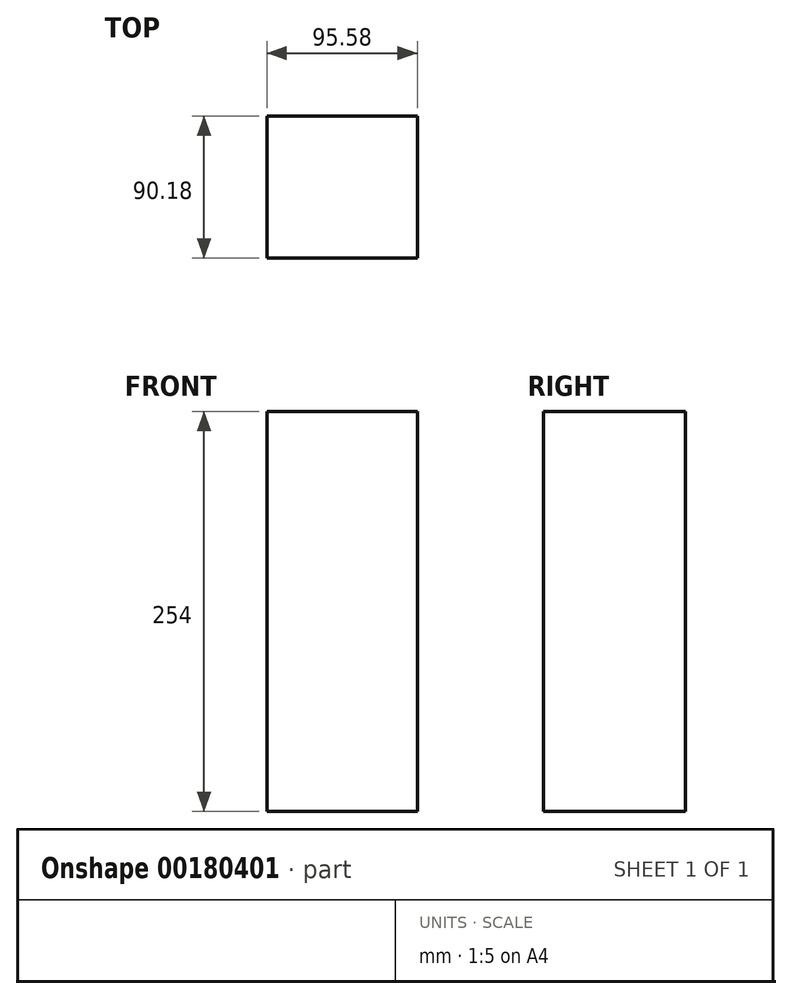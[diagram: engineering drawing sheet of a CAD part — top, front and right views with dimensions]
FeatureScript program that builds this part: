
annotation { "Feature Type Name" : "Feature", "Feature Type Description" : "" }
export const myFeature = defineFeature(function(context is Context, id is Id, definition is map)
    precondition{}
    {
        {
            var Q0;
            Q0=qCreatedBy(makeId("Top.planeOp"),FACE);
            var sketch = newSketch(context, id + "F0", { "sketchPlane" : qUnion([Q0])});
            skLineSegment(sketch, "E0.bottom", {"start": v(-77.6, 69.15) * mm, "end": v(17.97, 69.15) * mm});
            skLineSegment(sketch, "E0.top", {"start": v(-77.6, -21.03) * mm, "end": v(17.97, -21.03) * mm});
            skLineSegment(sketch, "E0.left", {"start": v(-77.6, 69.15) * mm, "end": v(-77.6, -21.03) * mm});
            skLineSegment(sketch, "E0.right", {"start": v(17.97, 69.15) * mm, "end": v(17.97, -21.03) * mm});
            skSolve(sketch);
        }
        {
            var Q0;
            Q0=qSketchRegion(id+"F0",true);
            extrude(context, id + "F1", {"entities" : qUnion([Q0]), "depth" : 254 * mm});
        }
    });
